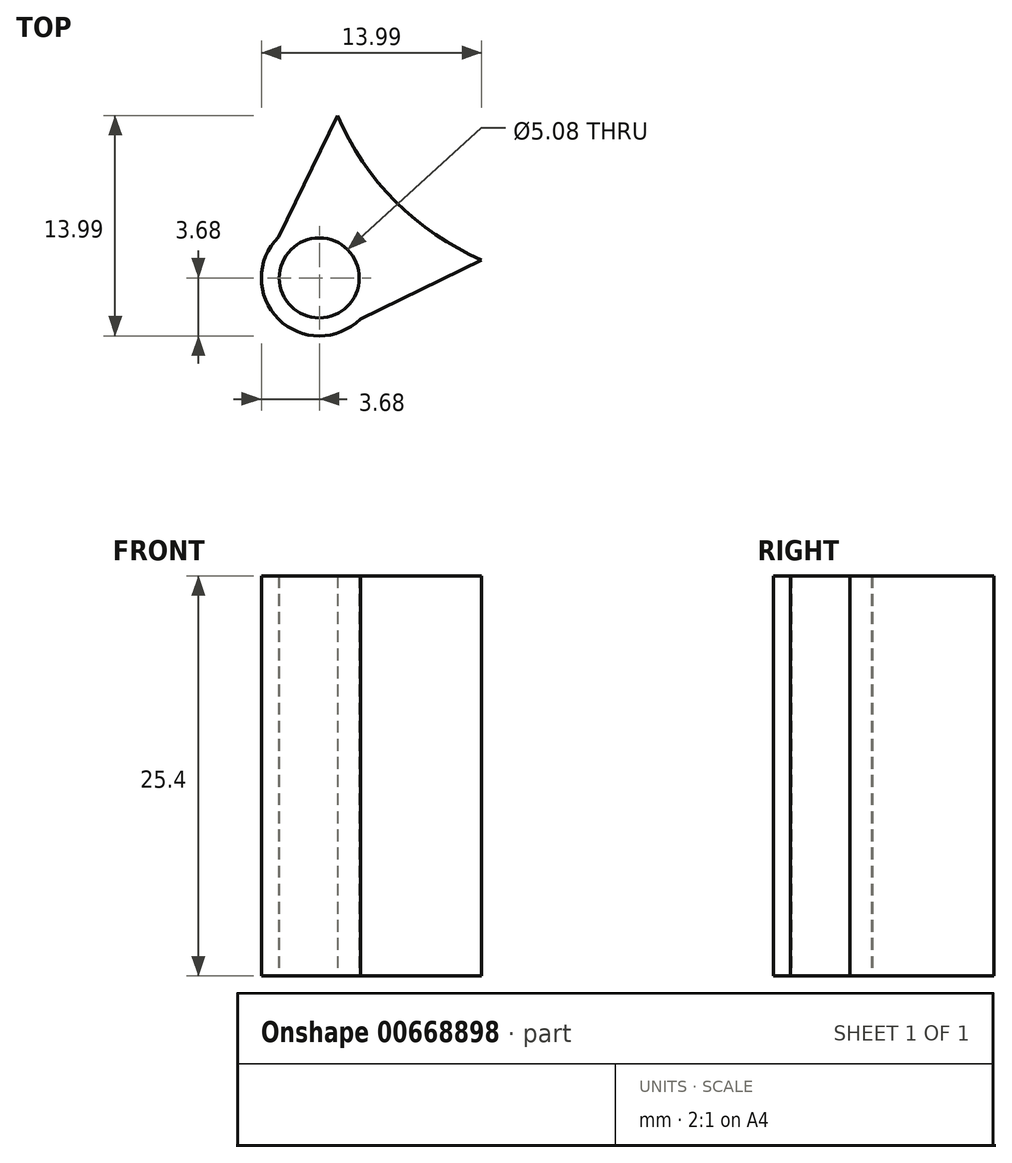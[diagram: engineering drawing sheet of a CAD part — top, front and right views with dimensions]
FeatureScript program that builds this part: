
annotation { "Feature Type Name" : "Feature", "Feature Type Description" : "" }
export const myFeature = defineFeature(function(context is Context, id is Id, definition is map)
    precondition{}
    {
        {
            var Q0;
            Q0=qCreatedBy(makeId("Top.planeOp"),FACE);
            var sketch = newSketch(context, id + "F0", { "sketchPlane" : qUnion([Q0])});
            skCircle(sketch, "E0", {"center": v(0, 0) * mm, "radius": 2.54 * mm});
            skArc(sketch, "E1", {"start": v(-2.6, 2.6) * mm, "mid": v(-2.6, -2.6) * mm, "end": v(2.6, -2.6) * mm});
            skLineSegment(sketch, "E2", {"start": v(-0.9, 6.1) * mm, "end": v(-2.6, 2.6) * mm});
            skLineSegment(sketch, "E3.MirrorCS", {"start": v(6.1, -0.9) * mm, "end": v(2.6, -2.6) * mm});
            skLineSegment(sketch, "E4", {"start": v(-0.9, 6.1) * mm, "end": v(-0.53, 6.87) * mm});
            skLineSegment(sketch, "E5.MirrorCS", {"start": v(6.1, -0.9) * mm, "end": v(6.87, -0.53) * mm});
            skPoint(sketch, "E6.MirrorCS.end.orphan", {"position": v(6.1, -0.9) * mm});
            skPoint(sketch, "E6.MirrorCS.start.orphan", {"position": v(5.2, 0) * mm});
            skPoint(sketch, "E7.orphan", {"position": v(0, 5.2) * mm});
            skPoint(sketch, "E8.orphan", {"position": v(-5.2, 0) * mm});
            skPoint(sketch, "E9.start.orphan", {"position": v(0, -5.2) * mm});
            skLineSegment(sketch, "E10", {"start": v(0, 0) * mm, "end": v(2.6, 2.6) * mm});
            skArc(sketch, "E11", {"start": v(1.15, 10.3) * mm, "mid": v(4.85, 4.85) * mm, "end": v(10.3, 1.15) * mm});
            skLineSegment(sketch, "E12", {"start": v(-0.53, 6.87) * mm, "end": v(1.15, 10.3) * mm});
            skLineSegment(sketch, "E13.MirrorCS", {"start": v(6.87, -0.53) * mm, "end": v(10.3, 1.15) * mm});
            skSolve(sketch);
        }
        {
            var Q0;
            Q0=makeQuery(id+"F0.imprint","IMPRINT",FACE,{"disambiguationData":[TD([[makeQuery(id+"F0.imprint","IMPRINT",EDGE,{"derivedFrom":sQuery(id+"F0.wireOp",EDGE,"E0")}),-1.0]])]});
            extrude(context, id + "F1", {"entities" : qUnion([Q0]), "depth" : 25.4 * mm, "offsetDistance" : 25.4 * mm});
        }
    });
